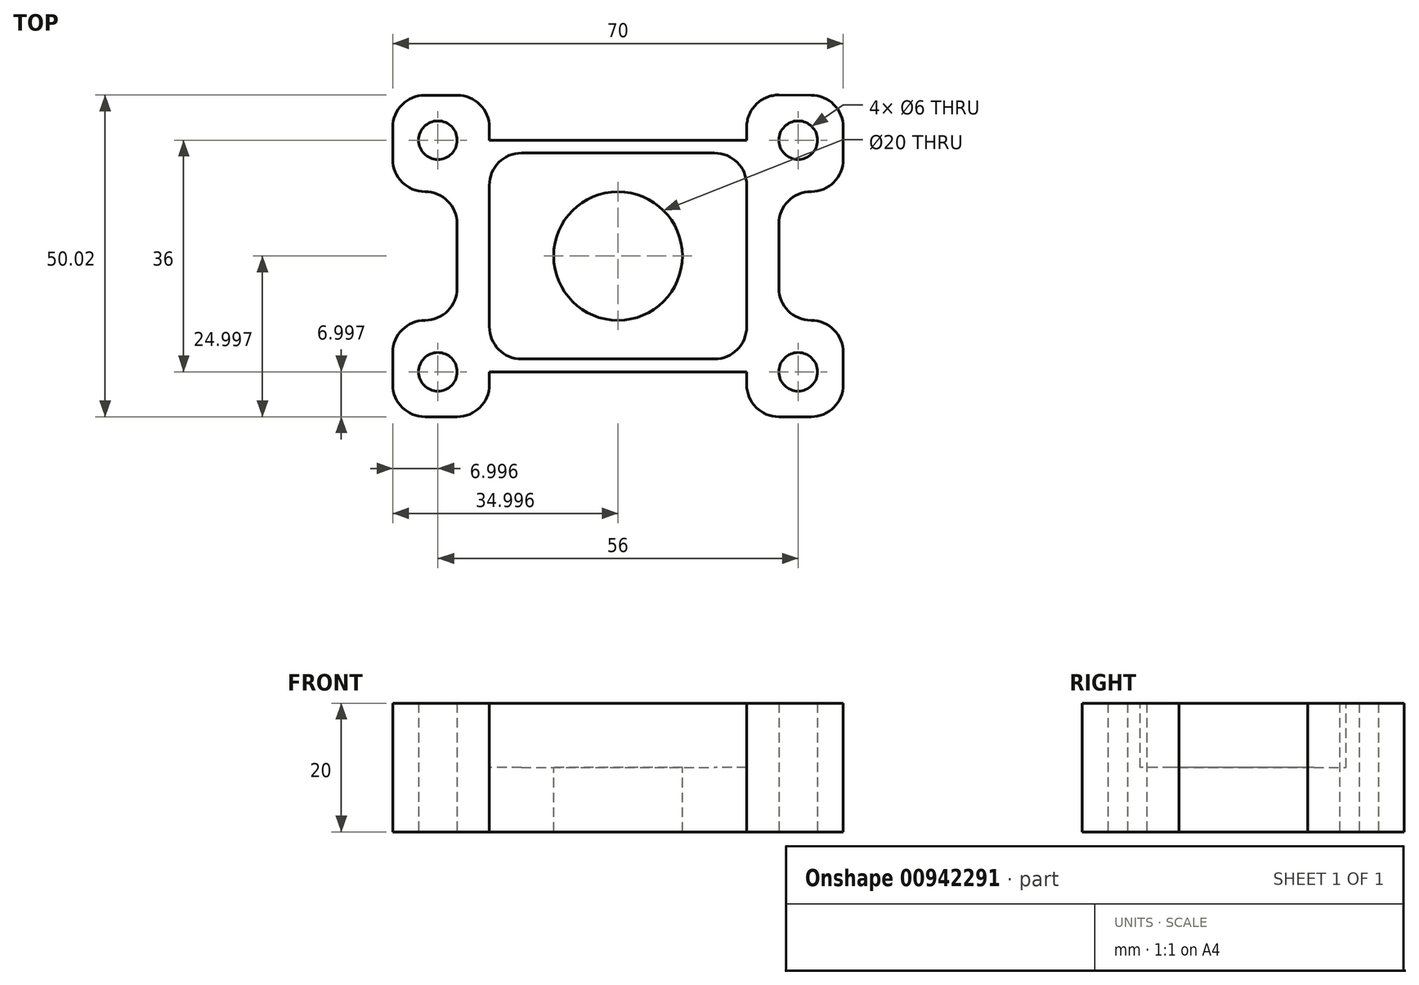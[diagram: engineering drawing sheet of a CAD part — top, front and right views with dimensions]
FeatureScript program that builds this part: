
annotation { "Feature Type Name" : "Feature", "Feature Type Description" : "" }
export const myFeature = defineFeature(function(context is Context, id is Id, definition is map)
    precondition{}
    {
        {
            var Q0;
            Q0=qCreatedBy(makeId("Top.planeOp"),FACE);
            var sketch = newSketch(context, id + "F0", { "sketchPlane" : qUnion([Q0])});
            skLineSegment(sketch, "E0.bottom", {"start": v(-21.24, 25.2) * mm, "end": v(-16.24, 25.2) * mm});
            skLineSegment(sketch, "E0.top", {"start": v(-21.24, -24.8) * mm, "end": v(-16.24, -24.8) * mm});
            skLineSegment(sketch, "E0.left", {"start": v(-26.24, 20.2) * mm, "end": v(-26.24, 15.2) * mm});
            skLineSegment(sketch, "E0.right", {"start": v(43.76, 20.2) * mm, "end": v(43.76, 15.2) * mm});
            skCircle(sketch, "E1", {"center": v(-19.24, 18.2) * mm, "radius": 3 * mm});
            skCircle(sketch, "E2", {"center": v(-19.24, -17.8) * mm, "radius": 3 * mm});
            skCircle(sketch, "E3", {"center": v(36.76, 18.2) * mm, "radius": 3 * mm});
            skCircle(sketch, "E4", {"center": v(36.76, -17.8) * mm, "radius": 3 * mm});
            skPoint(sketch, "E5.visualSharp", {"position": v(-26.24, 25.2) * mm});
            skArc(sketch, "E5.filletArc", {"start": v(-21.24, 25.2) * mm, "mid": v(-24.78, 23.74) * mm, "end": v(-26.24, 20.2) * mm});
            skPoint(sketch, "E6.visualSharp", {"position": v(43.76, 25.2) * mm});
            skArc(sketch, "E6.filletArc", {"start": v(43.76, 20.2) * mm, "mid": v(42.3, 23.74) * mm, "end": v(38.76, 25.2) * mm});
            skPoint(sketch, "E7.visualSharp", {"position": v(43.76, -24.8) * mm});
            skArc(sketch, "E7.filletArc", {"start": v(38.76, -24.8) * mm, "mid": v(42.3, -23.33) * mm, "end": v(43.76, -19.8) * mm});
            skPoint(sketch, "E8.visualSharp", {"position": v(-26.24, -24.8) * mm});
            skArc(sketch, "E8.filletArc", {"start": v(-26.24, -19.8) * mm, "mid": v(-24.78, -23.33) * mm, "end": v(-21.24, -24.8) * mm});
            skLineSegment(sketch, "E9.bottom", {"start": v(-21.24, 10.2) * mm, "end": v(-21.24, 10.2) * mm});
            skLineSegment(sketch, "E9.top", {"start": v(-21.24, -9.8) * mm, "end": v(-21.24, -9.8) * mm});
            skLineSegment(sketch, "E9.right", {"start": v(-16.24, 5.2) * mm, "end": v(-16.24, -4.8) * mm});
            skLineSegment(sketch, "E10.top", {"start": v(-11.24, -17.8) * mm, "end": v(28.76, -17.8) * mm});
            skLineSegment(sketch, "E10.left", {"start": v(-11.24, -19.8) * mm, "end": v(-11.24, -17.8) * mm});
            skLineSegment(sketch, "E10.right", {"start": v(28.76, -19.8) * mm, "end": v(28.76, -17.8) * mm});
            skLineSegment(sketch, "E11.bottom", {"start": v(38.76, 10.2) * mm, "end": v(38.76, 10.2) * mm});
            skLineSegment(sketch, "E11.top", {"start": v(38.76, -9.8) * mm, "end": v(38.76, -9.8) * mm});
            skLineSegment(sketch, "E11.right", {"start": v(33.76, 5.2) * mm, "end": v(33.76, -4.8) * mm});
            skLineSegment(sketch, "E12.trimOffspring", {"start": v(-26.24, -14.8) * mm, "end": v(-26.24, -19.8) * mm});
            skLineSegment(sketch, "E13.trimOffspring", {"start": v(43.76, -14.8) * mm, "end": v(43.76, -19.8) * mm});
            skLineSegment(sketch, "E14.trimOffspring", {"start": v(33.76, -24.8) * mm, "end": v(38.76, -24.8) * mm});
            skPoint(sketch, "E15.visualSharp", {"position": v(-26.24, -9.8) * mm});
            skArc(sketch, "E15.filletArc", {"start": v(-21.24, -9.8) * mm, "mid": v(-24.78, -11.26) * mm, "end": v(-26.24, -14.8) * mm});
            skPoint(sketch, "E16.visualSharp", {"position": v(-16.24, 10.2) * mm});
            skArc(sketch, "E16.filletArc", {"start": v(-16.24, 5.2) * mm, "mid": v(-17.7, 8.74) * mm, "end": v(-21.24, 10.2) * mm});
            skPoint(sketch, "E17.visualSharp", {"position": v(-26.24, 10.2) * mm});
            skArc(sketch, "E17.filletArc", {"start": v(-26.24, 15.2) * mm, "mid": v(-24.78, 11.67) * mm, "end": v(-21.24, 10.2) * mm});
            skPoint(sketch, "E18.visualSharp", {"position": v(-16.24, -9.8) * mm});
            skArc(sketch, "E18.filletArc", {"start": v(-21.24, -9.8) * mm, "mid": v(-17.7, -8.33) * mm, "end": v(-16.24, -4.8) * mm});
            skPoint(sketch, "E19.visualSharp", {"position": v(-11.24, 18.2) * mm});
            skPoint(sketch, "E20.visualSharp", {"position": v(28.76, 18.2) * mm});
            skPoint(sketch, "E21.visualSharp", {"position": v(33.76, 10.2) * mm});
            skArc(sketch, "E21.filletArc", {"start": v(38.76, 10.2) * mm, "mid": v(35.22, 8.74) * mm, "end": v(33.76, 5.2) * mm});
            skPoint(sketch, "E22.visualSharp", {"position": v(33.76, -9.8) * mm});
            skArc(sketch, "E22.filletArc", {"start": v(33.76, -4.8) * mm, "mid": v(35.22, -8.33) * mm, "end": v(38.76, -9.8) * mm});
            skPoint(sketch, "E23.visualSharp", {"position": v(-11.24, -24.8) * mm});
            skArc(sketch, "E23.filletArc", {"start": v(-16.24, -24.8) * mm, "mid": v(-12.7, -23.33) * mm, "end": v(-11.24, -19.8) * mm});
            skPoint(sketch, "E24.visualSharp", {"position": v(28.76, -24.8) * mm});
            skArc(sketch, "E24.filletArc", {"start": v(28.76, -19.8) * mm, "mid": v(30.22, -23.33) * mm, "end": v(33.76, -24.8) * mm});
            skPoint(sketch, "E25.visualSharp", {"position": v(43.76, -9.8) * mm});
            skArc(sketch, "E25.filletArc", {"start": v(43.76, -14.8) * mm, "mid": v(42.3, -11.26) * mm, "end": v(38.76, -9.8) * mm});
            skPoint(sketch, "E26.visualSharp", {"position": v(43.76, 10.2) * mm});
            skArc(sketch, "E26.filletArc", {"start": v(38.76, 10.2) * mm, "mid": v(42.3, 11.67) * mm, "end": v(43.76, 15.2) * mm});
            skPoint(sketch, "E27.visualSharp", {"position": v(-11.24, 25.2) * mm});
            skArc(sketch, "E27.filletArc", {"start": v(-11.24, 20.2) * mm, "mid": v(-12.7, 23.74) * mm, "end": v(-16.24, 25.2) * mm});
            skLineSegment(sketch, "E28", {"start": v(-11.24, 18.2) * mm, "end": v(28.76, 18.2) * mm});
            skLineSegment(sketch, "E29", {"start": v(-11.24, 20.2) * mm, "end": v(-11.24, 18.2) * mm});
            skLineSegment(sketch, "E30", {"start": v(28.76, 18.2) * mm, "end": v(28.76, 20.23) * mm});
            skLineSegment(sketch, "E31", {"start": v(33.78, 25.23) * mm, "end": v(38.76, 25.2) * mm});
            skPoint(sketch, "E32.visualSharp", {"position": v(28.76, 25.25) * mm});
            skArc(sketch, "E32.filletArc", {"start": v(33.78, 25.23) * mm, "mid": v(30.23, 23.77) * mm, "end": v(28.76, 20.23) * mm});
            skSolve(sketch);
        }
        {
            var Q0;
            Q0=makeQuery(id+"F0.imprint","IMPRINT",FACE,{"disambiguationData":[TD([[makeQuery(id+"F0.imprint","IMPRINT",EDGE,{"derivedFrom":sQuery(id+"F0.wireOp",EDGE,"E0.bottom")}),-1.0]])]});
            extrude(context, id + "F1", {"entities" : qUnion([Q0]), "depth" : 20 * mm, "offsetDistance" : 25 * mm});
        }
        {
            var Q0;
            Q0=makeQuery(id+"F1.opExtrude","CAP_FACE",FACE,{"disambiguationData":[OSD([sQuery(id+"F0.wireOp",EDGE,"E0.bottom"),sQuery(id+"F0.wireOp",EDGE,"E0.top"),sQuery(id+"F0.wireOp",EDGE,"E0.left"),sQuery(id+"F0.wireOp",EDGE,"E0.right"),sQuery(id+"F0.wireOp",EDGE,"E1"),sQuery(id+"F0.wireOp",EDGE,"E2"),sQuery(id+"F0.wireOp",EDGE,"E3"),sQuery(id+"F0.wireOp",EDGE,"E4")])],"isStart":false});
            var sketch = newSketch(context, id + "F2", { "sketchPlane" : qUnion([Q0])});
            skLineSegment(sketch, "E33.bottom", {"start": v(-6.24, 16.2) * mm, "end": v(23.76, 16.2) * mm});
            skLineSegment(sketch, "E33.top", {"start": v(-6.24, -15.8) * mm, "end": v(23.76, -15.8) * mm});
            skLineSegment(sketch, "E33.left", {"start": v(-11.24, 11.2) * mm, "end": v(-11.24, -10.8) * mm});
            skLineSegment(sketch, "E33.right", {"start": v(28.76, 11.2) * mm, "end": v(28.76, -10.8) * mm});
            skPoint(sketch, "E34.visualSharp", {"position": v(-11.24, 16.2) * mm});
            skArc(sketch, "E34.filletArc", {"start": v(-6.24, 16.2) * mm, "mid": v(-9.78, 14.74) * mm, "end": v(-11.24, 11.2) * mm});
            skPoint(sketch, "E35.visualSharp", {"position": v(28.76, 16.2) * mm});
            skArc(sketch, "E35.filletArc", {"start": v(28.76, 11.2) * mm, "mid": v(27.3, 14.74) * mm, "end": v(23.76, 16.2) * mm});
            skPoint(sketch, "E36.visualSharp", {"position": v(28.76, -15.8) * mm});
            skArc(sketch, "E36.filletArc", {"start": v(23.76, -15.8) * mm, "mid": v(27.3, -14.33) * mm, "end": v(28.76, -10.8) * mm});
            skPoint(sketch, "E37.visualSharp", {"position": v(-11.24, -15.8) * mm});
            skArc(sketch, "E37.filletArc", {"start": v(-11.24, -10.8) * mm, "mid": v(-9.78, -14.33) * mm, "end": v(-6.24, -15.8) * mm});
            skSolve(sketch);
        }
        {
            var Q0;
            Q0=makeQuery(id+"F2.imprint","IMPRINT",FACE,{"disambiguationData":[TD([[makeQuery(id+"F2.imprint","IMPRINT",EDGE,{"derivedFrom":sQuery(id+"F2.wireOp",EDGE,"E33.bottom")}),-1.0]])]});
            extrude(context, id + "F3", {"entities" : qUnion([Q0]), "operationType" : NewBodyOperationType.REMOVE, "oppositeDirection" : true, "depth" : 10 * mm, "offsetDistance" : 25 * mm});
        }
        {
            var Q0;
            Q0=makeQuery(id+"F3.boolean.opBoolean","COPY",FACE,{"derivedFrom":makeQuery(id+"F3.opExtrude","CAP_FACE",FACE,{"disambiguationData":[OSD([sQuery(id+"F2.wireOp",EDGE,"E33.bottom"),sQuery(id+"F2.wireOp",EDGE,"E33.top"),sQuery(id+"F2.wireOp",EDGE,"E33.left"),sQuery(id+"F2.wireOp",EDGE,"E33.right"),sQuery(id+"F2.wireOp",EDGE,"E34.filletArc"),sQuery(id+"F2.wireOp",EDGE,"E35.filletArc"),sQuery(id+"F2.wireOp",EDGE,"E36.filletArc"),sQuery(id+"F2.wireOp",EDGE,"E37.filletArc")])],"isStart":false})});
            var sketch = newSketch(context, id + "F4", { "sketchPlane" : qUnion([Q0])});
            skCircle(sketch, "E38", {"center": v(8.76, 0.2) * mm, "radius": 10 * mm});
            skSolve(sketch);
        }
        {
            var Q0;
            Q0=makeQuery(id+"F4.imprint","IMPRINT",FACE,{"disambiguationData":[TD([[makeQuery(id+"F4.imprint","IMPRINT",EDGE,{"derivedFrom":sQuery(id+"F4.wireOp",EDGE,"E38")}),1.0]])]});
            extrude(context, id + "F5", {"entities" : qUnion([Q0]), "operationType" : NewBodyOperationType.REMOVE, "oppositeDirection" : true, "depth" : 20 * mm, "offsetDistance" : 25 * mm});
        }
    });
